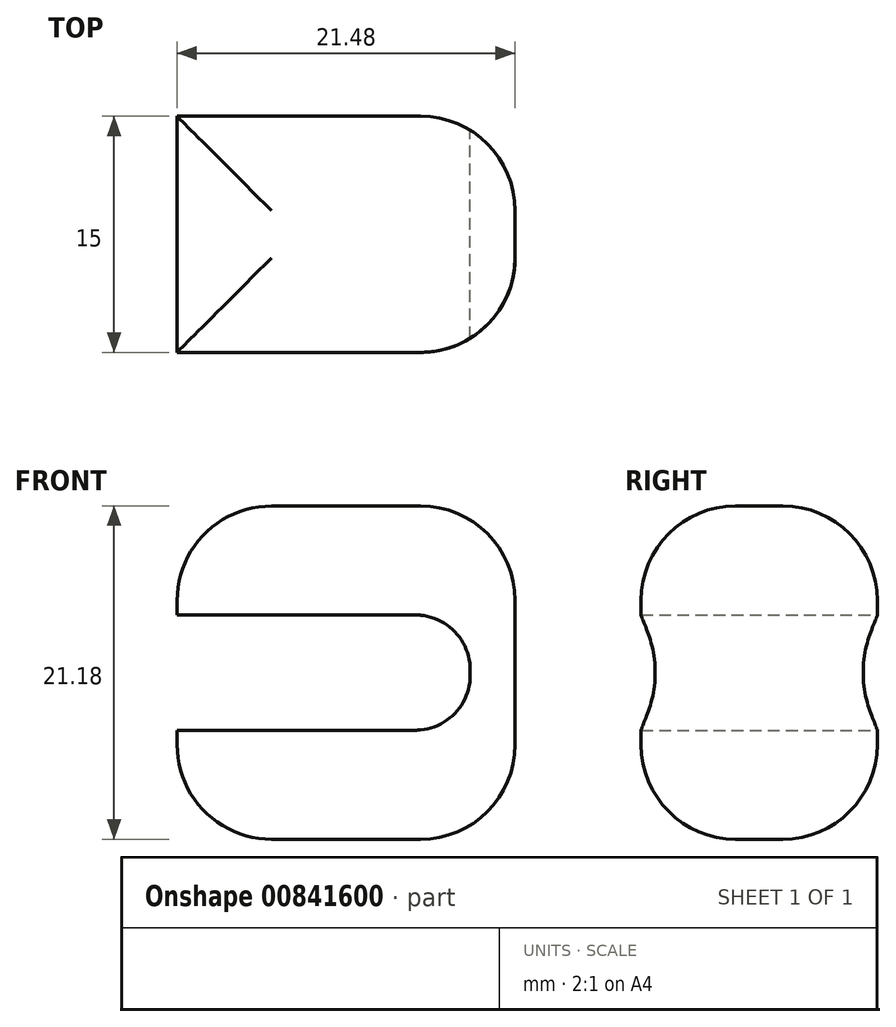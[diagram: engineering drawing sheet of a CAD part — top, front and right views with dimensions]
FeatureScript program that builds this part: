
annotation { "Feature Type Name" : "Feature", "Feature Type Description" : "" }
export const myFeature = defineFeature(function(context is Context, id is Id, definition is map)
    precondition{}
    {
        {
            var Q0;
            Q0=qCreatedBy(makeId("Front.planeOp"),FACE);
            var sketch = newSketch(context, id + "F0", { "sketchPlane" : qUnion([Q0])});
            skLineSegment(sketch, "E0.bottom", {"start": v(-10.74, 10.59) * mm, "end": v(10.74, 10.59) * mm});
            skLineSegment(sketch, "E0.top", {"start": v(-10.74, -10.59) * mm, "end": v(10.74, -10.59) * mm});
            skLineSegment(sketch, "E0.left", {"start": v(-10.74, 10.59) * mm, "end": v(-10.74, 3.66) * mm});
            skLineSegment(sketch, "E0.right", {"start": v(10.74, 10.59) * mm, "end": v(10.74, -10.59) * mm});
            skPoint(sketch, "E0.middle", {"position": v(0, 0) * mm});
            skLineSegment(sketch, "E1.bottom", {"start": v(-7.89, 3.66) * mm, "end": v(7.89, 3.66) * mm});
            skLineSegment(sketch, "E1.top", {"start": v(-7.89, -3.66) * mm, "end": v(7.89, -3.66) * mm});
            skLineSegment(sketch, "E1.right", {"start": v(7.89, 3.66) * mm, "end": v(7.89, -3.66) * mm});
            skLineSegment(sketch, "E2", {"start": v(-7.89, 3.66) * mm, "end": v(-10.74, 3.66) * mm});
            skLineSegment(sketch, "E3", {"start": v(-7.89, -3.66) * mm, "end": v(-10.74, -3.66) * mm});
            skLineSegment(sketch, "E4.trimOffspring", {"start": v(-10.74, -3.66) * mm, "end": v(-10.74, -10.59) * mm});
            skSolve(sketch);
        }
        {
            var Q0;
            Q0=makeQuery(id+"F0.imprint","IMPRINT",FACE,{"disambiguationData":[TD([[makeQuery(id+"F0.imprint","IMPRINT",EDGE,{"derivedFrom":sQuery(id+"F0.wireOp",EDGE,"E0.bottom")}),-1.0]])]});
            extrude(context, id + "F1", {"entities" : qUnion([Q0]), "depth" : 15 * mm, "offsetDistance" : 25 * mm});
        }
        {
            var Q0;
            Q0=makeQuery(id+"F1.opExtrude","SWEPT_EDGE",EDGE,{"disambiguationData":[OSD([sQuery(id+"F0.wireOp",EDGE,"E1.bottom"),sQuery(id+"F0.wireOp",EDGE,"E1.right")])]});
            var Q1;
            Q1=makeQuery(id+"F1.opExtrude","SWEPT_EDGE",EDGE,{"disambiguationData":[OSD([sQuery(id+"F0.wireOp",EDGE,"E1.top"),sQuery(id+"F0.wireOp",EDGE,"E1.right")])]});
            fillet(context, id + "F2", {"entities" : qUnion([Q0, Q1]), "radius" : 3.5 * mm, "tangentPropagation" : true, "allowEdgeOverflow" : false});
        }
        {
            var Q0;
            Q0=makeQuery(id+"F1.opExtrude","CAP_EDGE",EDGE,{"disambiguationData":[OSD([sQuery(id+"F0.wireOp",EDGE,"E0.top")])],"isStart":false});
            var Q1;
            Q1=makeQuery(id+"F1.opExtrude","CAP_EDGE",EDGE,{"disambiguationData":[OSD([sQuery(id+"F0.wireOp",EDGE,"E0.bottom")])],"isStart":false});
            var Q2;
            Q2=makeQuery(id+"F1.opExtrude","CAP_EDGE",EDGE,{"disambiguationData":[OSD([sQuery(id+"F0.wireOp",EDGE,"E0.right")])],"isStart":false});
            var Q3;
            Q3=makeQuery(id+"F1.opExtrude","CAP_EDGE",EDGE,{"disambiguationData":[OSD([sQuery(id+"F0.wireOp",EDGE,"E0.top")])],"isStart":true});
            var Q4;
            Q4=makeQuery(id+"F1.opExtrude","CAP_EDGE",EDGE,{"disambiguationData":[OSD([sQuery(id+"F0.wireOp",EDGE,"E0.bottom")])],"isStart":true});
            var Q5;
            Q5=makeQuery(id+"F1.opExtrude","CAP_EDGE",EDGE,{"disambiguationData":[OSD([sQuery(id+"F0.wireOp",EDGE,"E0.right")])],"isStart":true});
            var Q6;
            Q6=makeQuery(id+"F1.opExtrude","SWEPT_EDGE",EDGE,{"disambiguationData":[OSD([sQuery(id+"F0.wireOp",EDGE,"E0.top"),sQuery(id+"F0.wireOp",EDGE,"E4.trimOffspring")])]});
            var Q7;
            Q7=makeQuery(id+"F1.opExtrude","SWEPT_EDGE",EDGE,{"disambiguationData":[OSD([sQuery(id+"F0.wireOp",EDGE,"E0.bottom"),sQuery(id+"F0.wireOp",EDGE,"E0.left")])]});
            fillet(context, id + "F3", {"entities" : qUnion([Q0, Q1, Q2, Q3, Q4, Q5, Q6, Q7]), "radius" : 6 * mm, "tangentPropagation" : true, "allowEdgeOverflow" : false});
        }
        {
            var Q0;
            Q0=makeQuery(id+"F3.opFillet","BLEND_EDGE",EDGE,{"blendedFrom":[makeQuery(id+"F1.opExtrude","CAP_EDGE",EDGE,{"disambiguationData":[OSD([sQuery(id+"F0.wireOp",EDGE,"E0.top")])],"isStart":true}),makeQuery(id+"F1.opExtrude","CAP_EDGE",EDGE,{"disambiguationData":[OSD([sQuery(id+"F0.wireOp",EDGE,"E0.right")])],"isStart":true})],"blendedInto":[]});
            var Q1;
            Q1=makeQuery(id+"F3.opFillet","BLEND_EDGE",EDGE,{"blendedFrom":[makeQuery(id+"F1.opExtrude","CAP_EDGE",EDGE,{"disambiguationData":[OSD([sQuery(id+"F0.wireOp",EDGE,"E0.bottom")])],"isStart":true}),makeQuery(id+"F1.opExtrude","CAP_EDGE",EDGE,{"disambiguationData":[OSD([sQuery(id+"F0.wireOp",EDGE,"E0.right")])],"isStart":true})],"blendedInto":[]});
            fillet(context, id + "F4", {"entities" : qUnion([Q0, Q1]), "radius" : 6 * mm, "tangentPropagation" : true, "allowEdgeOverflow" : false});
        }
    });
